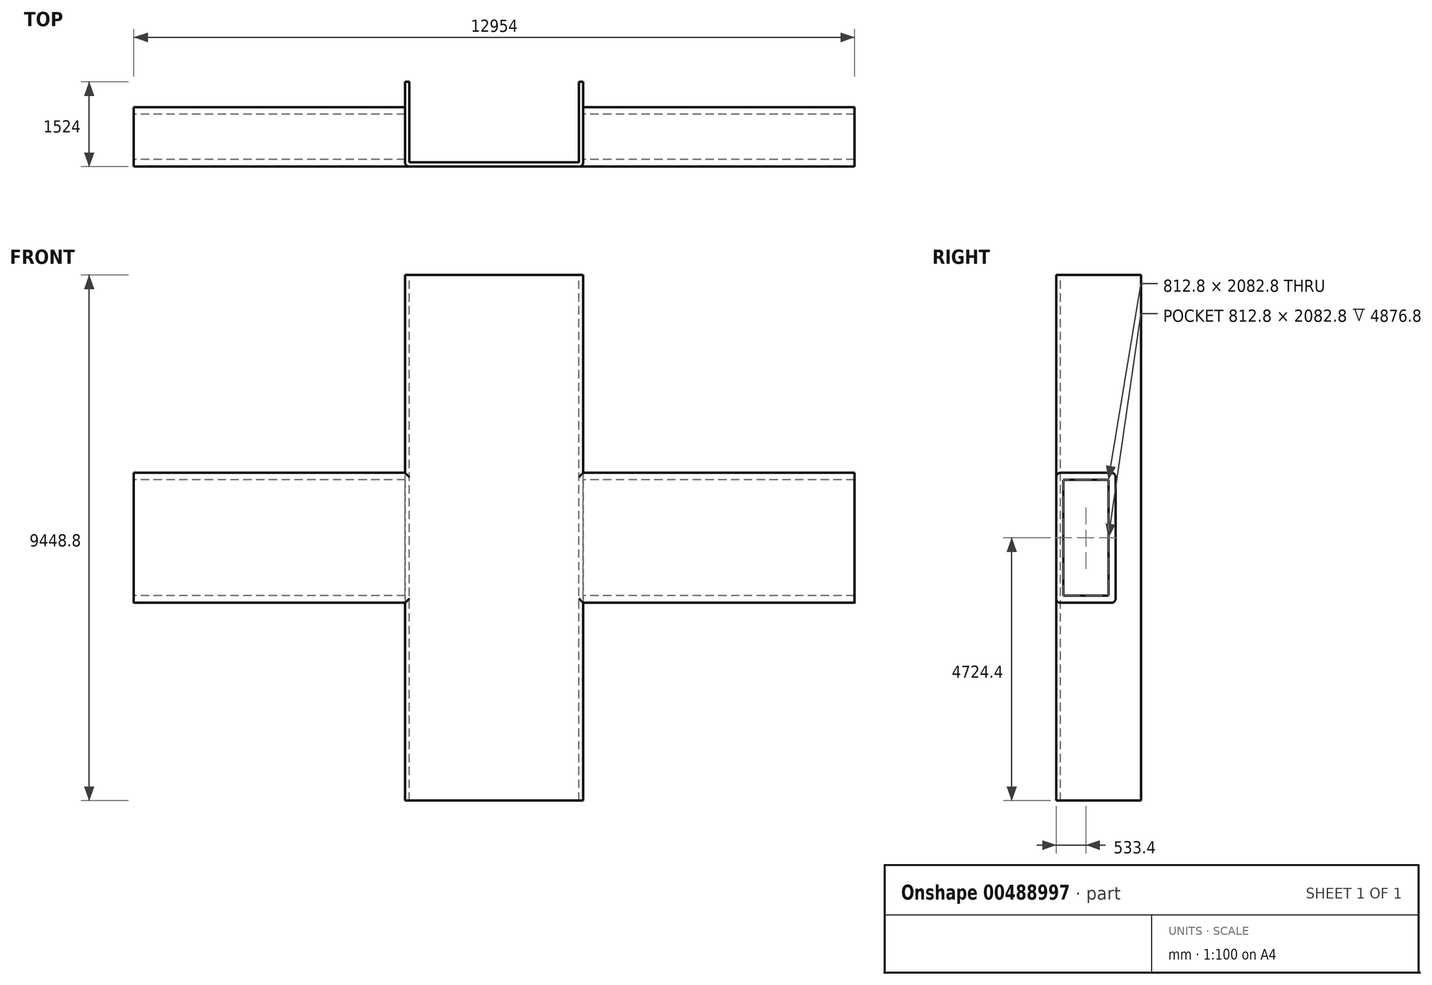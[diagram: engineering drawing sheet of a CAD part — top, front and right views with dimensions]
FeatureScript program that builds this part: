
annotation { "Feature Type Name" : "Feature", "Feature Type Description" : "" }
export const myFeature = defineFeature(function(context is Context, id is Id, definition is map)
    precondition{}
    {
        {
            var Q0;
            Q0=qCreatedBy(makeId("Right.planeOp"),FACE);
            var sketch = newSketch(context, id + "F0", { "sketchPlane" : qUnion([Q0])});
            skLineSegment(sketch, "E0.bottom", {"start": v(533.4, 1168.4) * mm, "end": v(-533.4, 1168.4) * mm});
            skLineSegment(sketch, "E0.top", {"start": v(533.4, -1168.4) * mm, "end": v(-533.4, -1168.4) * mm});
            skLineSegment(sketch, "E0.left", {"start": v(533.4, 1168.4) * mm, "end": v(533.4, -1168.4) * mm});
            skLineSegment(sketch, "E0.right", {"start": v(-533.4, 1168.4) * mm, "end": v(-533.4, -1168.4) * mm});
            skLineSegment(sketch, "E1.bottom", {"start": v(406.4, 1041.4) * mm, "end": v(-406.4, 1041.4) * mm});
            skLineSegment(sketch, "E1.top", {"start": v(406.4, -1041.4) * mm, "end": v(-406.4, -1041.4) * mm});
            skLineSegment(sketch, "E1.left", {"start": v(406.4, 1041.4) * mm, "end": v(406.4, -1041.4) * mm});
            skLineSegment(sketch, "E1.right", {"start": v(-406.4, 1041.4) * mm, "end": v(-406.4, -1041.4) * mm});
            skSolve(sketch);
        }
        {
            var Q0;
            Q0 = qSketchRegion(id + "F0", true);
            extrude(context, id + "F1", {"entities" : qUnion([Q0]), "endBound" : BoundingType.SYMMETRIC, "depth" : 12954 * mm});
        }
        {
            var Q0;
            Q0=qCreatedBy(makeId("Top.planeOp"),FACE);
            var sketch = newSketch(context, id + "F2", { "sketchPlane" : qUnion([Q0])});
            skLineSegment(sketch, "E2", {"start": v(1600.2, -533.4) * mm, "end": v(-1600.2, -533.4) * mm});
            skLineSegment(sketch, "E3", {"start": v(1600.2, -533.4) * mm, "end": v(1600.2, 990.6) * mm});
            skLineSegment(sketch, "E4", {"start": v(-1600.2, -533.4) * mm, "end": v(-1600.2, 990.6) * mm});
            skLineSegment(sketch, "E5", {"start": v(1600.2, 990.6) * mm, "end": v(-1600.2, 990.6) * mm});
            skSolve(sketch);
        }
        {
            var Q0;
            Q0 = qSketchRegion(id + "F2", true);
            extrude(context, id + "F3", {"entities" : qUnion([Q0]), "operationType" : NewBodyOperationType.ADD, "endBound" : BoundingType.SYMMETRIC, "depth" : 9448.8 * mm});
        }
        {
            var Q0;
            Q0=makeQuery(id+"F3.opExtrude","CAP_FACE",FACE,{"disambiguationData":[OSD([sQuery(id+"F2.wireOp",EDGE,"E2"),sQuery(id+"F2.wireOp",EDGE,"E3"),sQuery(id+"F2.wireOp",EDGE,"E4"),sQuery(id+"F2.wireOp",EDGE,"E5")])],"isStart":false});
            var sketch = newSketch(context, id + "F4", { "sketchPlane" : qUnion([Q0])});
            skLineSegment(sketch, "E6.bottom", {"start": v(1524, 990.6) * mm, "end": v(-1524, 990.6) * mm});
            skLineSegment(sketch, "E6.top", {"start": v(1524, -457.2) * mm, "end": v(-1524, -457.2) * mm});
            skLineSegment(sketch, "E6.left", {"start": v(1524, 990.6) * mm, "end": v(1524, -457.2) * mm});
            skLineSegment(sketch, "E6.right", {"start": v(-1524, 990.6) * mm, "end": v(-1524, -457.2) * mm});
            skSolve(sketch);
        }
        {
            var Q0;
            Q0 = qSketchRegion(id + "F4", true);
            extrude(context, id + "F5", {"entities" : qUnion([Q0]), "operationType" : NewBodyOperationType.REMOVE, "oppositeDirection" : true, "depth" : 9448.8 * mm});
        }
        {
            var Q0;
            {var subQ0=sQuery(id+"F0.wireOp",EDGE,"E0.right");var subQ1=sQuery(id+"F0.wireOp",EDGE,"E0.bottom");Q0=makeQuery(id+"F3.boolean.opBoolean","SPLIT",EDGE,{"disambiguationData":[TD([makeQuery(id+"F3.opExtrude","SWEPT_FACE",FACE,{"disambiguationData":[OSD([sQuery(id+"F2.wireOp",EDGE,"E4")])]})])],"derivedFrom":makeQuery(id+"F1.opExtrude","SWEPT_EDGE",EDGE,{"disambiguationData":[OSD([subQ1,subQ0])]})});}
            var Q1;
            {var subQ0=sQuery(id+"F0.wireOp",EDGE,"E0.right");var subQ1=sQuery(id+"F0.wireOp",EDGE,"E0.top");Q1=makeQuery(id+"F3.boolean.opBoolean","SPLIT",EDGE,{"disambiguationData":[TD([makeQuery(id+"F3.opExtrude","SWEPT_FACE",FACE,{"disambiguationData":[OSD([sQuery(id+"F2.wireOp",EDGE,"E4")])]})])],"derivedFrom":makeQuery(id+"F1.opExtrude","SWEPT_EDGE",EDGE,{"disambiguationData":[OSD([subQ1,subQ0])]})});}
            var Q2;
            {var subQ0=sQuery(id+"F2.wireOp",EDGE,"E4");var subQ1=sQuery(id+"F2.wireOp",EDGE,"E2");Q2=makeQuery(id+"F3.boolean.opBoolean","SPLIT",EDGE,{"disambiguationData":[TD([makeQuery(id+"F1.opExtrude","SWEPT_FACE",FACE,{"disambiguationData":[OSD([sQuery(id+"F0.wireOp",EDGE,"E0.top")])]})])],"derivedFrom":makeQuery(id+"F3.opExtrude","SWEPT_EDGE",EDGE,{"disambiguationData":[OSD([subQ1,subQ0])]})});}
            var Q3;
            {var subQ0=sQuery(id+"F2.wireOp",EDGE,"E3");var subQ1=sQuery(id+"F2.wireOp",EDGE,"E2");Q3=makeQuery(id+"F3.boolean.opBoolean","SPLIT",EDGE,{"disambiguationData":[TD([makeQuery(id+"F1.opExtrude","SWEPT_FACE",FACE,{"disambiguationData":[OSD([sQuery(id+"F0.wireOp",EDGE,"E0.top")])]})])],"derivedFrom":makeQuery(id+"F3.opExtrude","SWEPT_EDGE",EDGE,{"disambiguationData":[OSD([subQ1,subQ0])]})});}
            var Q4;
            {var subQ0=sQuery(id+"F0.wireOp",EDGE,"E0.right");var subQ1=sQuery(id+"F0.wireOp",EDGE,"E0.top");Q4=makeQuery(id+"F3.boolean.opBoolean","SPLIT",EDGE,{"disambiguationData":[TD([makeQuery(id+"F3.opExtrude","SWEPT_FACE",FACE,{"disambiguationData":[OSD([sQuery(id+"F2.wireOp",EDGE,"E3")])]})])],"derivedFrom":makeQuery(id+"F1.opExtrude","SWEPT_EDGE",EDGE,{"disambiguationData":[OSD([subQ1,subQ0])]})});}
            var Q5;
            {var subQ0=sQuery(id+"F0.wireOp",EDGE,"E0.right");var subQ1=sQuery(id+"F0.wireOp",EDGE,"E0.bottom");Q5=makeQuery(id+"F3.boolean.opBoolean","SPLIT",EDGE,{"disambiguationData":[TD([makeQuery(id+"F3.opExtrude","SWEPT_FACE",FACE,{"disambiguationData":[OSD([sQuery(id+"F2.wireOp",EDGE,"E3")])]})])],"derivedFrom":makeQuery(id+"F1.opExtrude","SWEPT_EDGE",EDGE,{"disambiguationData":[OSD([subQ1,subQ0])]})});}
            var Q6;
            {var subQ0=sQuery(id+"F2.wireOp",EDGE,"E2");var subQ1=sQuery(id+"F2.wireOp",EDGE,"E3");Q6=makeQuery(id+"F3.boolean.opBoolean","SPLIT",EDGE,{"disambiguationData":[TD([makeQuery(id+"F1.opExtrude","SWEPT_FACE",FACE,{"disambiguationData":[OSD([sQuery(id+"F0.wireOp",EDGE,"E0.bottom")])]})])],"derivedFrom":makeQuery(id+"F3.opExtrude","SWEPT_EDGE",EDGE,{"disambiguationData":[OSD([subQ0,subQ1])]})});}
            var Q7;
            {var subQ0=sQuery(id+"F2.wireOp",EDGE,"E2");var subQ1=sQuery(id+"F2.wireOp",EDGE,"E4");Q7=makeQuery(id+"F3.boolean.opBoolean","SPLIT",EDGE,{"disambiguationData":[TD([makeQuery(id+"F1.opExtrude","SWEPT_FACE",FACE,{"disambiguationData":[OSD([sQuery(id+"F0.wireOp",EDGE,"E0.bottom")])]})])],"derivedFrom":makeQuery(id+"F3.opExtrude","SWEPT_EDGE",EDGE,{"disambiguationData":[OSD([subQ0,subQ1])]})});}
            var Q8;
            {var subQ0=sQuery(id+"F0.wireOp",EDGE,"E0.bottom");var subQ1=sQuery(id+"F0.wireOp",EDGE,"E0.left");Q8=makeQuery(id+"F3.boolean.opBoolean","SPLIT",EDGE,{"disambiguationData":[TD([makeQuery(id+"F3.opExtrude","SWEPT_FACE",FACE,{"disambiguationData":[OSD([sQuery(id+"F2.wireOp",EDGE,"E4")])]})])],"derivedFrom":makeQuery(id+"F1.opExtrude","SWEPT_EDGE",EDGE,{"disambiguationData":[OSD([subQ0,subQ1])]})});}
            var Q9;
            {var subQ0=sQuery(id+"F0.wireOp",EDGE,"E0.left");var subQ1=sQuery(id+"F0.wireOp",EDGE,"E0.top");Q9=makeQuery(id+"F3.boolean.opBoolean","SPLIT",EDGE,{"disambiguationData":[TD([makeQuery(id+"F3.opExtrude","SWEPT_FACE",FACE,{"disambiguationData":[OSD([sQuery(id+"F2.wireOp",EDGE,"E4")])]})])],"derivedFrom":makeQuery(id+"F1.opExtrude","SWEPT_EDGE",EDGE,{"disambiguationData":[OSD([subQ1,subQ0])]})});}
            var Q10;
            {var subQ0=sQuery(id+"F0.wireOp",EDGE,"E0.bottom");var subQ1=sQuery(id+"F0.wireOp",EDGE,"E0.left");Q10=makeQuery(id+"F3.boolean.opBoolean","SPLIT",EDGE,{"disambiguationData":[TD([makeQuery(id+"F3.opExtrude","SWEPT_FACE",FACE,{"disambiguationData":[OSD([sQuery(id+"F2.wireOp",EDGE,"E3")])]})])],"derivedFrom":makeQuery(id+"F1.opExtrude","SWEPT_EDGE",EDGE,{"disambiguationData":[OSD([subQ0,subQ1])]})});}
            var Q11;
            {var subQ0=sQuery(id+"F0.wireOp",EDGE,"E0.left");var subQ1=sQuery(id+"F0.wireOp",EDGE,"E0.top");Q11=makeQuery(id+"F3.boolean.opBoolean","SPLIT",EDGE,{"disambiguationData":[TD([makeQuery(id+"F3.opExtrude","SWEPT_FACE",FACE,{"disambiguationData":[OSD([sQuery(id+"F2.wireOp",EDGE,"E3")])]})])],"derivedFrom":makeQuery(id+"F1.opExtrude","SWEPT_EDGE",EDGE,{"disambiguationData":[OSD([subQ1,subQ0])]})});}
            fillet(context, id + "F6", {"entities" : qUnion([Q0, Q1, Q2, Q3, Q4, Q5, Q6, Q7, Q8, Q9, Q10, Q11]), "radius" : 76.2 * mm, "tangentPropagation" : true, "allowEdgeOverflow" : false});
        }
    });
